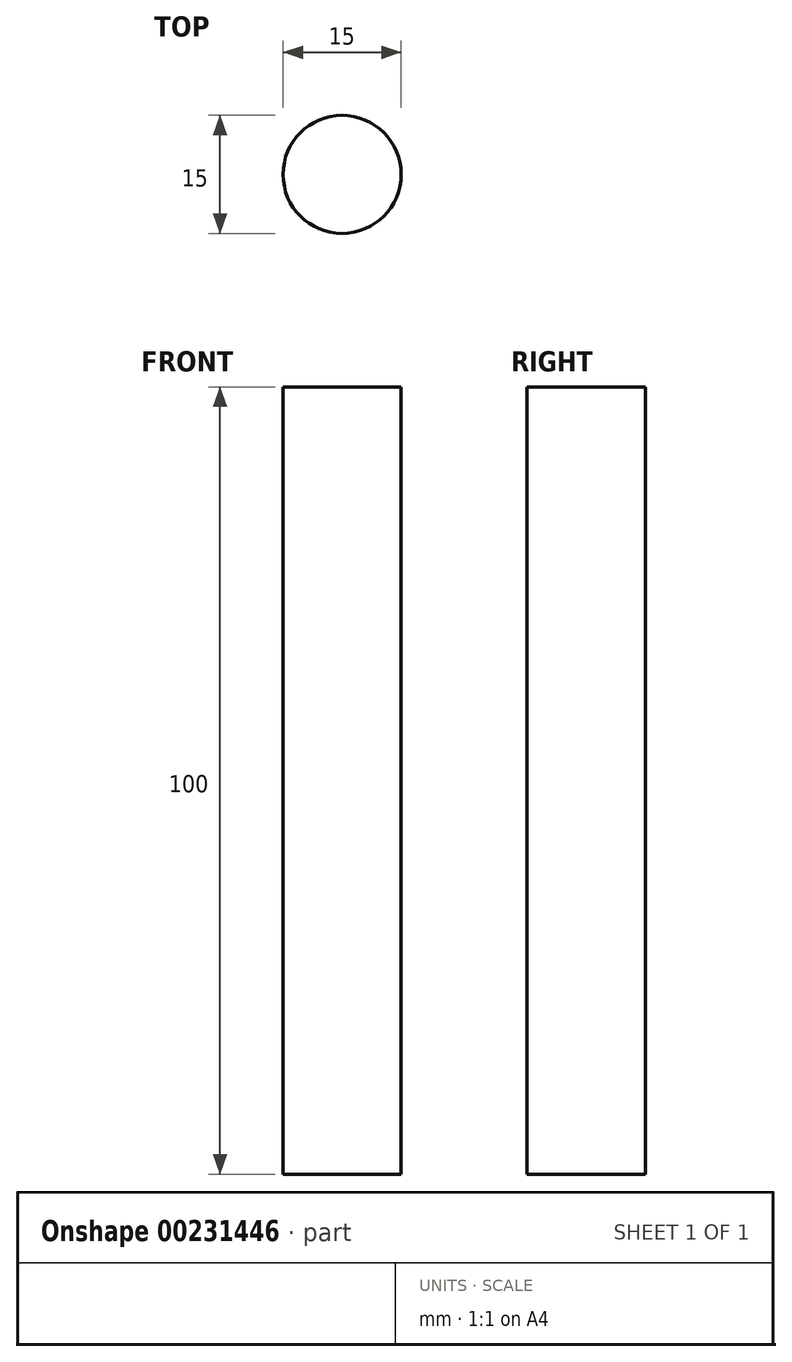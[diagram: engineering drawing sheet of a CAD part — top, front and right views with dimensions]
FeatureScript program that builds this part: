
annotation { "Feature Type Name" : "Feature", "Feature Type Description" : "" }
export const myFeature = defineFeature(function(context is Context, id is Id, definition is map)
    precondition{}
    {
        {
            var Q0;
            Q0=qCreatedBy(makeId("Top.planeOp"),FACE);
            var sketch = newSketch(context, id + "F0", { "sketchPlane" : qUnion([Q0])});
            skCircle(sketch, "E0", {"center": v(0, 0) * mm, "radius": 7.5 * mm});
            skSolve(sketch);
        }
        {
            var Q0;
            Q0 = qSketchRegion(id + "F0", true);
            extrude(context, id + "F1", {"entities" : qUnion([Q0]), "depth" : 100 * mm});
        }
    });
